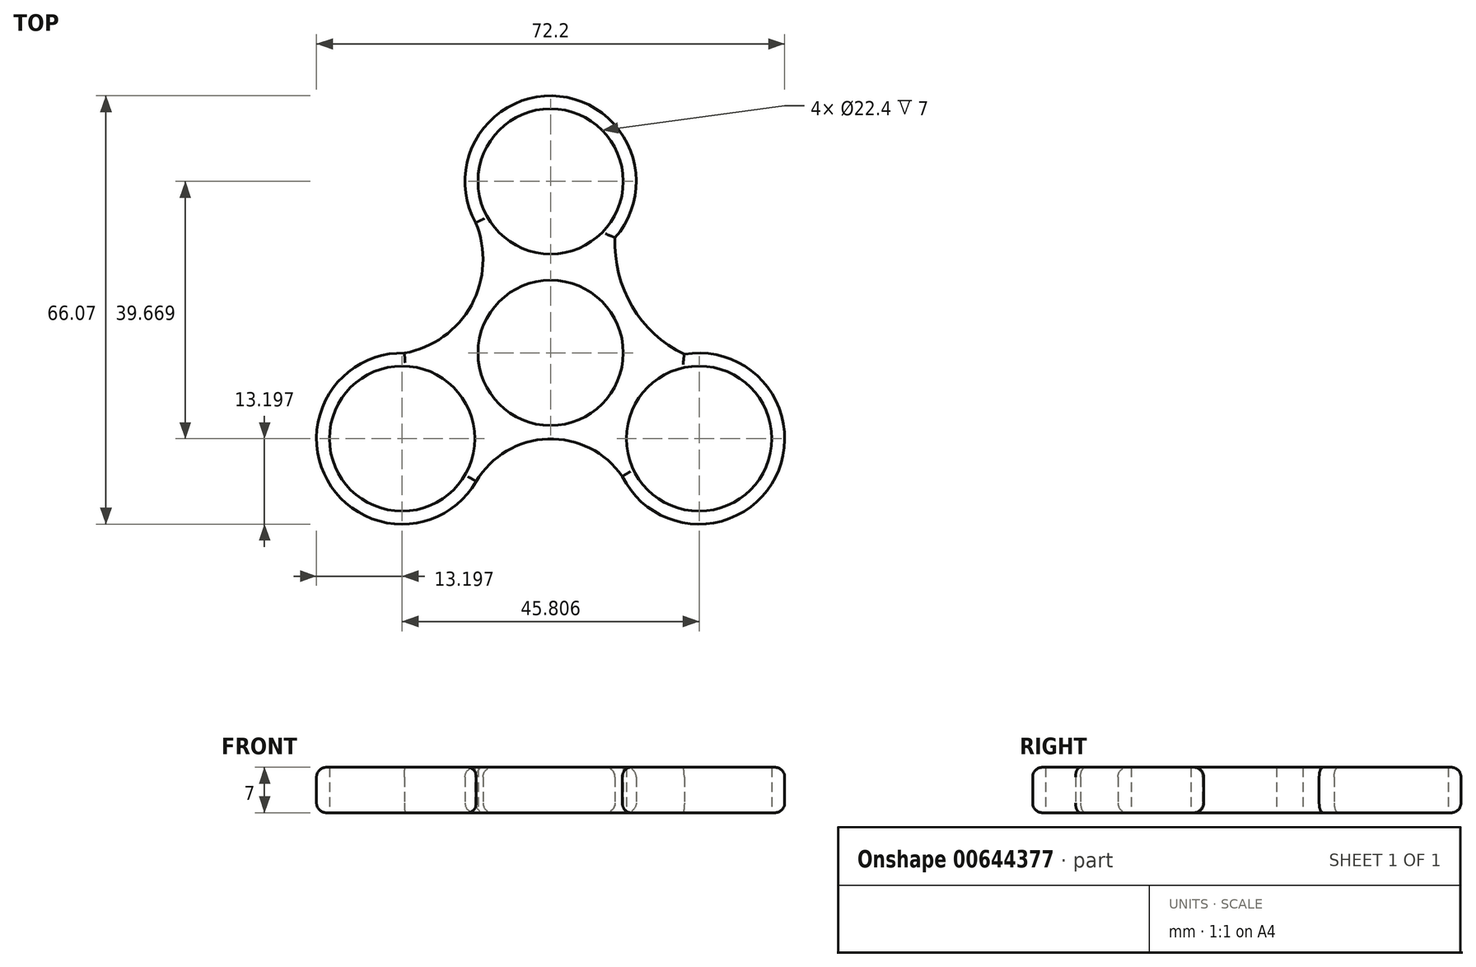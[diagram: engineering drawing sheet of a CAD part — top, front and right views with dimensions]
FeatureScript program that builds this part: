
annotation { "Feature Type Name" : "Feature", "Feature Type Description" : "" }
export const myFeature = defineFeature(function(context is Context, id is Id, definition is map)
    precondition{}
    {
        {
            var Q0;
            Q0=qCreatedBy(makeId("Top.planeOp"),FACE);
            var sketch = newSketch(context, id + "F0", { "sketchPlane" : qUnion([Q0])});
            skCircle(sketch, "E0", {"center": v(0, 0) * mm, "radius": 11.2 * mm});
            skCircle(sketch, "E1", {"center": v(0, 26.45) * mm, "radius": 11.2 * mm});
            skArc(sketch, "E2", {"start": v(9.94, 17.76) * mm, "mid": v(1.4, 39.57) * mm, "end": v(-11.56, 20.07) * mm});
            skArc(sketch, "E3.1.0", {"start": v(-22.54, -0.03) * mm, "mid": v(-34.42, -19.67) * mm, "end": v(-11.47, -19.82) * mm});
            skCircle(sketch, "E3.1.1", {"center": v(-22.9, -13.22) * mm, "radius": 11.2 * mm});
            skArc(sketch, "E3.2.0", {"start": v(11.05, -19.04) * mm, "mid": v(34.67, -19.2) * mm, "end": v(20.62, -0.22) * mm});
            skCircle(sketch, "E3.2.1", {"center": v(22.9, -13.22) * mm, "radius": 11.2 * mm});
            skArc(sketch, "E4", {"start": v(-22.54, -0.03) * mm, "mid": v(-12.21, 7.38) * mm, "end": v(-11.56, 20.07) * mm});
            skArc(sketch, "E5", {"start": v(9.94, 17.76) * mm, "mid": v(12.57, 7.16) * mm, "end": v(20.62, -0.22) * mm});
            skArc(sketch, "E6", {"start": v(11.05, -19.04) * mm, "mid": v(-0.5, -13.28) * mm, "end": v(-11.56, -19.97) * mm});
            skSolve(sketch);
        }
        {
            var Q0;
            Q0 = qSketchRegion(id + "F0", true);
            extrude(context, id + "F1", {"entities" : qUnion([Q0]), "depth" : 7 * mm, "offsetDistance" : 25 * mm});
        }
        {
            var Q0;
            Q0=makeQuery(id+"F1.opExtrude","CAP_EDGE",EDGE,{"disambiguationData":[OSD([sQuery(id+"F0.wireOp",EDGE,"E4")])],"isStart":false});
            var Q1;
            Q1=makeQuery(id+"F1.opExtrude","CAP_EDGE",EDGE,{"disambiguationData":[OSD([sQuery(id+"F0.wireOp",EDGE,"E2")])],"isStart":false});
            var Q2;
            Q2=makeQuery(id+"F1.opExtrude","CAP_EDGE",EDGE,{"disambiguationData":[OSD([sQuery(id+"F0.wireOp",EDGE,"E5")])],"isStart":false});
            var Q3;
            Q3=makeQuery(id+"F1.opExtrude","CAP_EDGE",EDGE,{"disambiguationData":[OSD([sQuery(id+"F0.wireOp",EDGE,"E3.2.0")])],"isStart":false});
            var Q4;
            Q4=makeQuery(id+"F1.opExtrude","CAP_EDGE",EDGE,{"disambiguationData":[OSD([sQuery(id+"F0.wireOp",EDGE,"E6")])],"isStart":false});
            var Q5;
            Q5=makeQuery(id+"F1.opExtrude","CAP_EDGE",EDGE,{"disambiguationData":[OSD([sQuery(id+"F0.wireOp",EDGE,"E3.1.0")])],"isStart":false});
            fillet(context, id + "F2", {"entities" : qUnion([Q0, Q1, Q2, Q3, Q4, Q5]), "radius" : 1.5 * mm, "tangentPropagation" : true, "allowEdgeOverflow" : false});
        }
        {
            var Q0;
            Q0=makeQuery(id+"F1.opExtrude","CAP_EDGE",EDGE,{"disambiguationData":[OSD([sQuery(id+"F0.wireOp",EDGE,"E6")])],"isStart":true});
            var Q1;
            Q1=makeQuery(id+"F1.opExtrude","CAP_EDGE",EDGE,{"disambiguationData":[OSD([sQuery(id+"F0.wireOp",EDGE,"E5")])],"isStart":true});
            var Q2;
            Q2=makeQuery(id+"F1.opExtrude","CAP_EDGE",EDGE,{"disambiguationData":[OSD([sQuery(id+"F0.wireOp",EDGE,"E3.2.0")])],"isStart":true});
            var Q3;
            Q3=makeQuery(id+"F1.opExtrude","CAP_EDGE",EDGE,{"disambiguationData":[OSD([sQuery(id+"F0.wireOp",EDGE,"E2")])],"isStart":true});
            var Q4;
            Q4=makeQuery(id+"F1.opExtrude","CAP_EDGE",EDGE,{"disambiguationData":[OSD([sQuery(id+"F0.wireOp",EDGE,"E4")])],"isStart":true});
            var Q5;
            Q5=makeQuery(id+"F1.opExtrude","CAP_EDGE",EDGE,{"disambiguationData":[OSD([sQuery(id+"F0.wireOp",EDGE,"E3.1.0")])],"isStart":true});
            fillet(context, id + "F3", {"entities" : qUnion([Q0, Q1, Q2, Q3, Q4, Q5]), "radius" : 1.5 * mm, "tangentPropagation" : true, "allowEdgeOverflow" : false});
        }
    });
